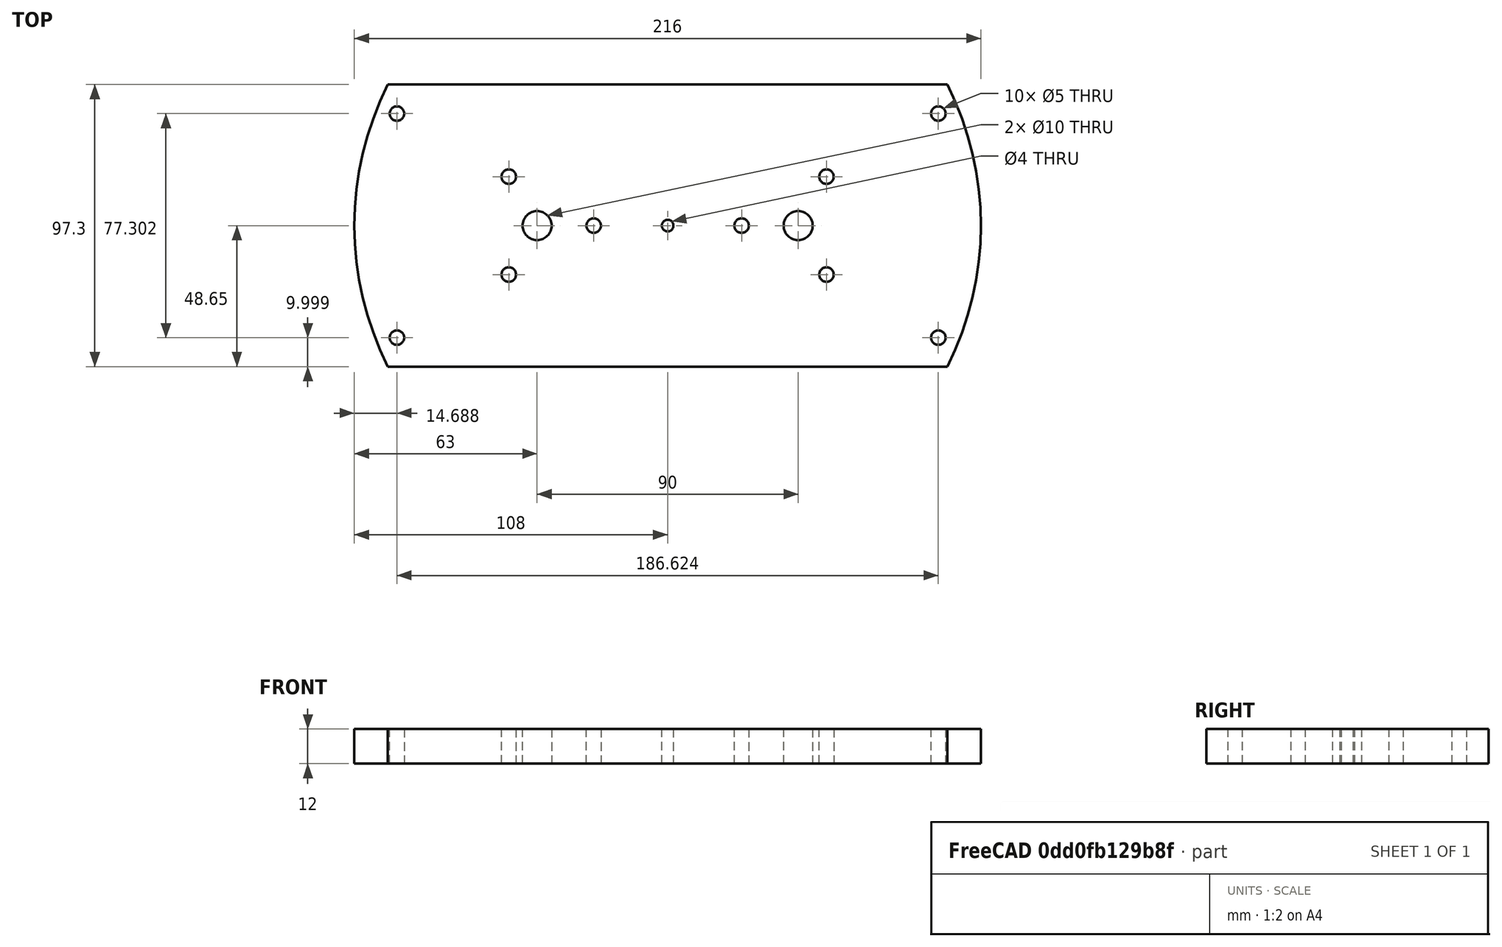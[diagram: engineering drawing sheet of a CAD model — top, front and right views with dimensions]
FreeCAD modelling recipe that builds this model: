
FCSTD DOCUMENT  (FreeCAD 0.19R24276 (Git))
Label: Out_gear_holder_for_CNC_H12_middle_parts_from_part16_as4_Plate_2bear_holder
License: All rights reserved
LicenseURL: http://en.wikipedia.org/wiki/All_rights_reserved
objects: Sketcher::SketchObject×1, PartDesign::Pad×1, PartDesign::Body×1
note: 4 computed .brp shape members not serialized (recipe doc carries the construction recipe); baked Part::Feature solids carry a one-line shape summary decoded from their .brp

FEATURE [Sketcher::SketchObject] Sketch001  label="Sketch001_d190_d216"
  FullyConstrained = true
  MapMode = 5
  Placement = pos=(0,0,0) rot=(1,0,0;3.14159rad)
  sketch-geometry (43):
    g0: Circle CenterX=0 CenterY=0 CenterZ=0 NormalX=0 NormalY=0 NormalZ=1 AngleXU=0 Radius=95
    g1: Circle CenterX=0 CenterY=0 CenterZ=0 NormalX=0 NormalY=0 NormalZ=1 AngleXU=0 Radius=95
    g2: Circle CenterX=0 CenterY=0 CenterZ=0 NormalX=0 NormalY=0 NormalZ=1 AngleXU=0 Radius=108
    g3: Circle CenterX=0 CenterY=0 CenterZ=0 NormalX=0 NormalY=0 NormalZ=1 AngleXU=0 Radius=101
    g4: LineSegment StartX=0 StartY=0 StartZ=0 EndX=93.3118 EndY=38.651 EndZ=0
    g5: LineSegment StartX=0 StartY=0 StartZ=0 EndX=-93.3118 EndY=38.651 EndZ=0
    g6: LineSegment StartX=0 StartY=0 StartZ=0 EndX=-93.3118 EndY=-38.651 EndZ=0
    g7: LineSegment StartX=0 StartY=0 StartZ=0 EndX=38.651 EndY=93.3118 EndZ=0
    g8: LineSegment StartX=0 StartY=0 StartZ=0 EndX=-38.651 EndY=-93.3118 EndZ=0
    g9: LineSegment StartX=0 StartY=0 StartZ=0 EndX=-38.651 EndY=93.3118 EndZ=0
    g10: LineSegment StartX=0 StartY=0 StartZ=0 EndX=38.651 EndY=-93.3118 EndZ=0
    g11: LineSegment StartX=0 StartY=0 StartZ=0 EndX=93.3118 EndY=-38.651 EndZ=0
    g12: Circle CenterX=38.651 CenterY=93.3118 CenterZ=0 NormalX=0 NormalY=0 NormalZ=1 AngleXU=0 Radius=2.5
    g13: Circle CenterX=93.3118 CenterY=38.651 CenterZ=0 NormalX=0 NormalY=0 NormalZ=1 AngleXU=0 Radius=2.5
    g14: Circle CenterX=93.3118 CenterY=-38.651 CenterZ=0 NormalX=0 NormalY=0 NormalZ=1 AngleXU=0 Radius=2.5
    g15: Circle CenterX=38.651 CenterY=-93.3118 CenterZ=0 NormalX=0 NormalY=0 NormalZ=1 AngleXU=0 Radius=2.5
    g16: Circle CenterX=-38.651 CenterY=93.3118 CenterZ=0 NormalX=0 NormalY=0 NormalZ=1 AngleXU=0 Radius=2.5
    g17: Circle CenterX=-93.3118 CenterY=38.651 CenterZ=0 NormalX=0 NormalY=0 NormalZ=1 AngleXU=0 Radius=2.5
    g18: Circle CenterX=-93.3118 CenterY=-38.651 CenterZ=0 NormalX=0 NormalY=0 NormalZ=1 AngleXU=0 Radius=2.5
    g19: Circle CenterX=-38.651 CenterY=-93.3118 CenterZ=0 NormalX=0 NormalY=0 NormalZ=1 AngleXU=0 Radius=2.5
    g20: LineSegment StartX=-96.4214 StartY=48.651 StartZ=0 EndX=96.4214 EndY=48.651 EndZ=0
    g21: LineSegment StartX=96.4214 StartY=-48.651 StartZ=0 EndX=-96.4214 EndY=-48.651 EndZ=0
    g22: Circle CenterX=-45 CenterY=0 CenterZ=0 NormalX=0 NormalY=0 NormalZ=1 AngleXU=0 Radius=5
    g23: Circle CenterX=45 CenterY=0 CenterZ=0 NormalX=0 NormalY=0 NormalZ=1 AngleXU=0 Radius=5
    g24: LineSegment StartX=25.5 StartY=0 StartZ=0 EndX=54.75 EndY=-16.8875 EndZ=0
    g25: LineSegment StartX=54.75 StartY=-16.8875 StartZ=0 EndX=54.75 EndY=16.8875 EndZ=0
    g26: LineSegment StartX=54.75 StartY=16.8875 StartZ=0 EndX=25.5 EndY=0 EndZ=0
    g27: Circle CenterX=45 CenterY=0 CenterZ=0 NormalX=0 NormalY=0 NormalZ=1 AngleXU=0 Radius=19.5
    g28: LineSegment StartX=-25.5 StartY=0 StartZ=0 EndX=-54.75 EndY=16.8875 EndZ=0
    g29: LineSegment StartX=-54.75 StartY=16.8875 StartZ=0 EndX=-54.75 EndY=-16.8875 EndZ=0
    g30: LineSegment StartX=-54.75 StartY=-16.8875 StartZ=0 EndX=-25.5 EndY=0 EndZ=0
    g31: Circle CenterX=-45 CenterY=0 CenterZ=0 NormalX=0 NormalY=0 NormalZ=1 AngleXU=0 Radius=19.5
    g32: Circle CenterX=54.75 CenterY=16.8875 CenterZ=0 NormalX=0 NormalY=0 NormalZ=1 AngleXU=0 Radius=2.5
    g33: Circle CenterX=25.5 CenterY=0 CenterZ=0 NormalX=0 NormalY=0 NormalZ=1 AngleXU=0 Radius=2.5
    g34: Circle CenterX=54.75 CenterY=-16.8875 CenterZ=0 NormalX=0 NormalY=0 NormalZ=1 AngleXU=0 Radius=2.5
    g35: Circle CenterX=-54.75 CenterY=16.8875 CenterZ=0 NormalX=0 NormalY=0 NormalZ=1 AngleXU=0 Radius=2.5
    g36: Circle CenterX=-25.5 CenterY=0 CenterZ=0 NormalX=0 NormalY=0 NormalZ=1 AngleXU=0 Radius=2.5
    g37: Circle CenterX=-54.75 CenterY=-16.8875 CenterZ=0 NormalX=0 NormalY=0 NormalZ=1 AngleXU=0 Radius=2.5
    g38: Circle CenterX=-45 CenterY=0 CenterZ=0 NormalX=0 NormalY=0 NormalZ=1 AngleXU=0 Radius=30
    g39: Circle CenterX=45 CenterY=0 CenterZ=0 NormalX=0 NormalY=0 NormalZ=1 AngleXU=0 Radius=30
    g40: ArcOfCircle CenterX=0 CenterY=0 CenterZ=0 NormalX=0 NormalY=0 NormalZ=1 AngleXU=0 Radius=108 StartAngle=2.6743 EndAngle=3.60889
    g41: ArcOfCircle CenterX=0 CenterY=0 CenterZ=0 NormalX=0 NormalY=0 NormalZ=1 AngleXU=0 Radius=108 StartAngle=5.81589 EndAngle=6.75048
    g42: Circle CenterX=0 CenterY=0 CenterZ=0 NormalX=0 NormalY=0 NormalZ=1 AngleXU=0 Radius=2
  constraints (106):
    c: Coincident(g0,g-1)
    c: Diameter(g0) = 190
    c: Coincident(g1,g0)
    c: Diameter(g1) = 190
    c: Coincident(g2,g1)
    c: Diameter(g2) = 216
    c: Coincident(g3,g1)
    c: Diameter(g3) = 202
    c: Coincident(g4,g1)
    c: Coincident(g5,g1)
    c: Coincident(g6,g1)
    c: Parallel(g6,g4)
    c: Coincident(g7,g1)
    c: Coincident(g8,g1)
    c: Parallel(g8,g7)
    c: Coincident(g9,g1)
    c: Coincident(g10,g1)
    c: Parallel(g10,g9)
    c: PointOnObject(g7,g3)
    c: PointOnObject(g4,g3)
    c: PointOnObject(g9,g3)
    c: PointOnObject(g5,g3)
    c: PointOnObject(g6,g3)
    c: PointOnObject(g8,g3)
    c: PointOnObject(g10,g3)
    c: Coincident(g11,g1)
    c: Parallel(g5,g11)
    c: PointOnObject(g11,g3)
    c: Angle(g-1,g4) = 0.392699
    c: Angle(g4,g7) = 0.785398
    c: Angle(g11,g-1) = 0.392699
    c: Angle(g10,g11) = 0.785398
    c: Coincident(g12,g7)
    c: Coincident(g13,g4)
    c: Coincident(g14,g11)
    c: Coincident(g15,g10)
    c: Diameter(g15) = 5
    c: Equal(g15,g14)
    c: Equal(g15,g13)
    c: Equal(g15,g12)
    c: Diameter(g19) = 5
    c: Equal(g19,g18)
    c: Equal(g19,g17)
    c: Equal(g19,g16)
    c: Horizontal(g20)
    c: Horizontal(g21)
    c: PointOnObject(g22,g-1)
    c: PointOnObject(g23,g-1)
    c: DistanceX(g22,g1) = 45
    c: DistanceX(g1,g23) = 45
    c: Coincident(g24,g25)
    c: Coincident(g25,g26)
    c: Coincident(g26,g24)
    c: Equal(g24,g25)
    c: Equal(g24,g26)
    c: PointOnObject(g24,g27)
    c: PointOnObject(g25,g27)
    c: PointOnObject(g26,g27)
    c: Coincident(g27,g23)
    c: PointOnObject(g26,g-1)
    c: Diameter(g27) = 39
    c: Diameter(g23) = 10
    c: Equal(g22,g23)
    c: Coincident(g28,g29)
    c: Coincident(g29,g30)
    c: Coincident(g30,g28)
    c: Equal(g28,g29)
    c: Equal(g28,g30)
    c: PointOnObject(g28,g31)
    c: PointOnObject(g29,g31)
    c: PointOnObject(g30,g31)
    c: Coincident(g31,g22)
    c: PointOnObject(g30,g-1)
    c: Equal(g31,g27)
    c: Coincident(g32,g25)
    c: Coincident(g33,g24)
    c: Coincident(g34,g24)
    c: Coincident(g35,g28)
    c: Coincident(g36,g28)
    c: Coincident(g37,g29)
    c: Diameter(g35) = 5
    c: Equal(g35,g37)
    c: Equal(g35,g36)
    c: Equal(g35,g33)
    c: Equal(g35,g32)
    c: Equal(g35,g34)
    c: Coincident(g38,g22)
    c: Coincident(g39,g23)
    c: Diameter(g39) = 60
    c: Equal(g39,g38)
    c: Coincident(g5,g17)
    c: Coincident(g18,g6)
    c: Coincident(g16,g9)
    c: Coincident(g19,g8)
    c: Coincident(g40,g-1)
    c: DistanceY(g17,g20) = 10
    c: DistanceY(g21,g18) = 10
    c: Coincident(g40,g20)
    c: Coincident(g41,g20)
    c: Equal(g40,g41)
    c: Coincident(g40,g21)
    c: Coincident(g41,g21)
    c: Coincident(g40,g41)
    c: Diameter(g41) = 216
    c: Coincident(g42,g40)
    c: Diameter(g42) = 4
FEATURE [PartDesign::Pad] Pad  label="Pad_H12"
  Direction = (1,1,1)
  Length = 12
  Length2 = 100
  Placement = pos=(0,0,0) rot=(1,0,0;3.14159rad)
  Profile = -> Sketch001
  Type = 0
FEATURE [PartDesign::Body] Body
  Group = -> [Sketch001,Pad]
  Origin = -> Origin
  Tip = -> Pad
